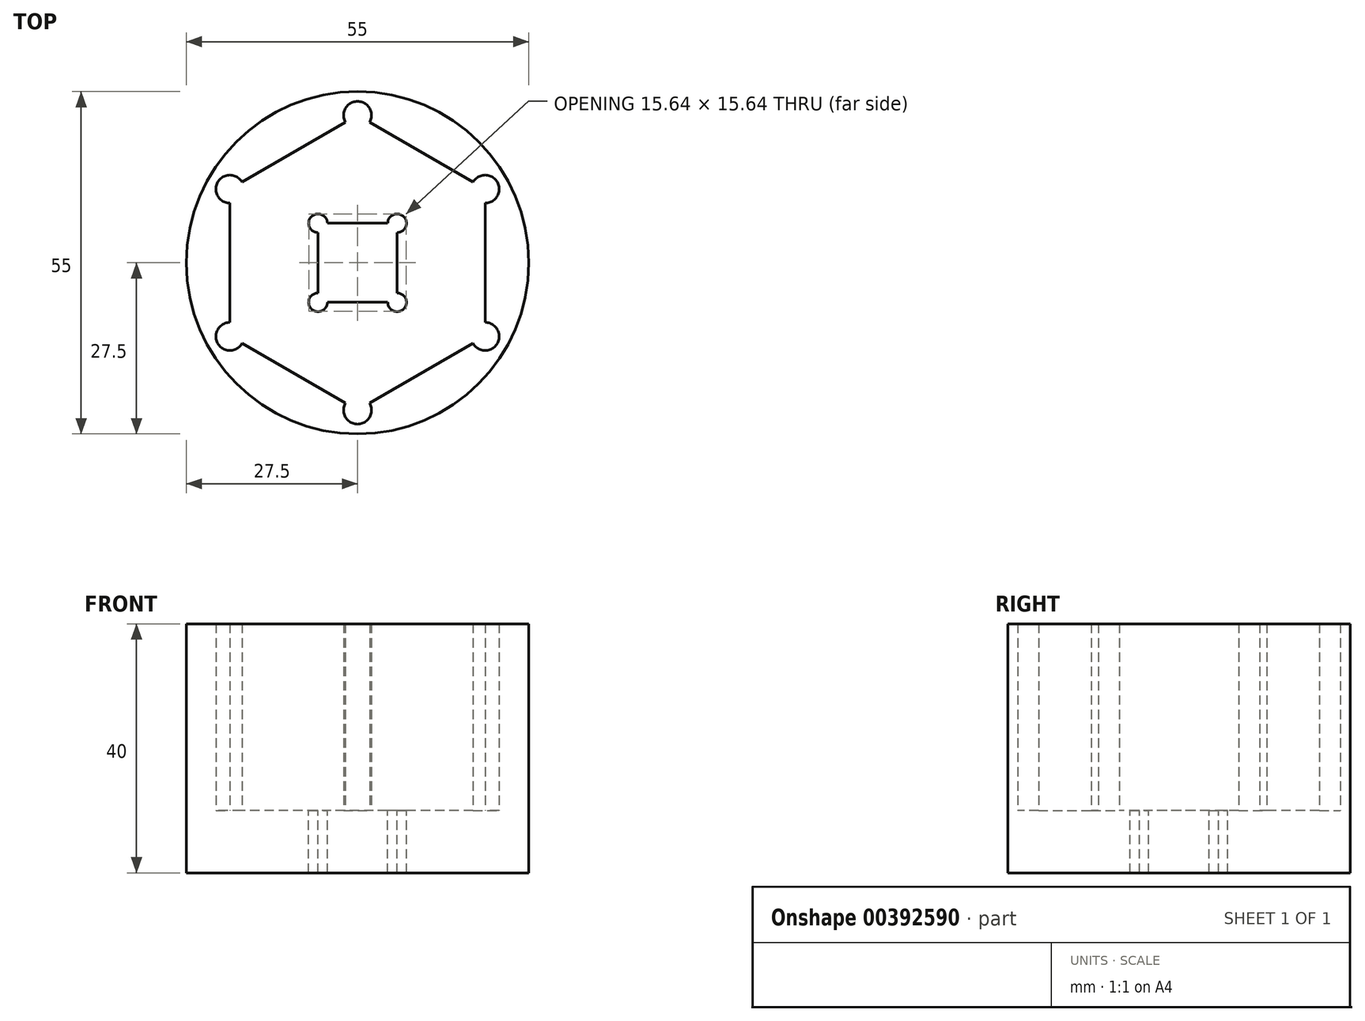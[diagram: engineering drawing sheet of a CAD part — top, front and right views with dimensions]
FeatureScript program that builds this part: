
annotation { "Feature Type Name" : "Feature", "Feature Type Description" : "" }
export const myFeature = defineFeature(function(context is Context, id is Id, definition is map)
    precondition{}
    {
        {
            var Q0;
            Q0=qCreatedBy(makeId("Top.planeOp"),FACE);
            var sketch = newSketch(context, id + "F0", { "sketchPlane" : qUnion([Q0])});
            skCircle(sketch, "E0", {"center": v(0, 0) * mm, "radius": 27.5 * mm});
            skCircle(sketch, "E1.cCircle", {"center": v(0, 0) * mm, "radius": 20.5 * mm, "construction": true});
            skLineSegment(sketch, "E1.0", {"start": v(20.5, 11.84) * mm, "end": v(20.5, -11.84) * mm});
            skLineSegment(sketch, "E1.1", {"start": v(20.5, -11.84) * mm, "end": v(0, -23.67) * mm});
            skLineSegment(sketch, "E1.2", {"start": v(0, -23.67) * mm, "end": v(-20.5, -11.84) * mm});
            skLineSegment(sketch, "E1.3", {"start": v(-20.5, -11.84) * mm, "end": v(-20.5, 11.84) * mm});
            skLineSegment(sketch, "E1.4", {"start": v(-20.5, 11.84) * mm, "end": v(0, 23.67) * mm});
            skLineSegment(sketch, "E1.5", {"start": v(0, 23.67) * mm, "end": v(20.5, 11.84) * mm});
            skPoint(sketch, "E1.0.midPoint", {"position": v(20.5, 0) * mm});
            skCircle(sketch, "E2", {"center": v(-20.5, -11.84) * mm, "radius": 2.25 * mm});
            skCircle(sketch, "E3", {"center": v(-20.5, 11.84) * mm, "radius": 2.25 * mm});
            skCircle(sketch, "E4", {"center": v(0, 23.67) * mm, "radius": 2.25 * mm});
            skCircle(sketch, "E5", {"center": v(20.5, 11.84) * mm, "radius": 2.25 * mm});
            skCircle(sketch, "E6", {"center": v(20.5, -11.84) * mm, "radius": 2.25 * mm});
            skCircle(sketch, "E7", {"center": v(0, -23.67) * mm, "radius": 2.25 * mm});
            skCircle(sketch, "E8", {"center": v(-16.6, -9.59) * mm, "radius": 3.9 * mm, "construction": true});
            skPoint(sketch, "E9", {"position": v(-18.55, -12.96) * mm});
            skPoint(sketch, "E10", {"position": v(-20.5, -9.59) * mm});
            skCircle(sketch, "E11", {"center": v(0, 0) * mm, "radius": 20 * mm, "construction": true});
            skLineSegment(sketch, "E12.bottom", {"start": v(6.35, 6.35) * mm, "end": v(-6.35, 6.35) * mm});
            skLineSegment(sketch, "E12.top", {"start": v(6.35, -6.35) * mm, "end": v(-6.35, -6.35) * mm});
            skLineSegment(sketch, "E12.left", {"start": v(6.35, 6.35) * mm, "end": v(6.35, -6.35) * mm});
            skLineSegment(sketch, "E12.right", {"start": v(-6.35, 6.35) * mm, "end": v(-6.35, -6.35) * mm});
            skCircle(sketch, "E13", {"center": v(-6.35, 6.35) * mm, "radius": 1.5 * mm});
            skCircle(sketch, "E14", {"center": v(6.35, 6.35) * mm, "radius": 1.5 * mm});
            skCircle(sketch, "E15", {"center": v(6.35, -6.35) * mm, "radius": 1.5 * mm});
            skCircle(sketch, "E16", {"center": v(-6.35, -6.35) * mm, "radius": 1.5 * mm});
            skCircle(sketch, "E17", {"center": v(0, 0) * mm, "radius": 6 * mm, "construction": true});
            skSolve(sketch);
        }
        {
            var Q0;
            {var subQ19=sQuery(id+"F0.wireOp",EDGE,"E5");var subQ21=sQuery(id+"F0.wireOp",EDGE,"E1.0");var subQ22=makeQuery(id+"F0.imprint","INTERSECT",VERTEX,{"derivedFrom":[subQ21,subQ19]});Q0=makeQuery(id+"F0.imprint","IMPRINT",FACE,{"disambiguationData":[TD([[makeQuery(id+"F0.imprint","IMPRINT",EDGE,{"disambiguationData":[TD([[subQ22,-1.0]])],"derivedFrom":subQ21}),-1.0]])]});}
            var Q1;
            Q1=makeQuery(id+"F0.imprint","IMPRINT",FACE,{"disambiguationData":[TD([[makeQuery(id+"F0.imprint","IMPRINT",EDGE,{"derivedFrom":sQuery(id+"F0.wireOp",EDGE,"E0")}),1.0]])]});
            var Q2;
            {var subQ0=sQuery(id+"F0.wireOp",EDGE,"E1.4");var subQ1=sQuery(id+"F0.wireOp",EDGE,"E1.3");var subQ2=makeQuery(id+"F0.imprint","INTERSECT",VERTEX,{"derivedFrom":[subQ1,subQ0]});Q2=makeQuery(id+"F0.imprint","IMPRINT",FACE,{"disambiguationData":[TD([[makeQuery(id+"F0.imprint","IMPRINT",EDGE,{"disambiguationData":[TD([[subQ2,1.0]])],"derivedFrom":subQ1}),1.0]])]});}
            var Q3;
            {var subQ0=sQuery(id+"F0.wireOp",EDGE,"E1.3");var subQ1=sQuery(id+"F0.wireOp",EDGE,"E1.2");var subQ2=makeQuery(id+"F0.imprint","INTERSECT",VERTEX,{"derivedFrom":[subQ1,subQ0]});Q3=makeQuery(id+"F0.imprint","IMPRINT",FACE,{"disambiguationData":[TD([[makeQuery(id+"F0.imprint","IMPRINT",EDGE,{"disambiguationData":[TD([[subQ2,1.0]])],"derivedFrom":subQ1}),1.0]])]});}
            var Q4;
            {var subQ0=sQuery(id+"F0.wireOp",EDGE,"E1.3");var subQ1=sQuery(id+"F0.wireOp",EDGE,"E1.2");var subQ2=makeQuery(id+"F0.imprint","INTERSECT",VERTEX,{"derivedFrom":[subQ1,subQ0]});Q4=makeQuery(id+"F0.imprint","IMPRINT",FACE,{"disambiguationData":[TD([[makeQuery(id+"F0.imprint","IMPRINT",EDGE,{"disambiguationData":[TD([[subQ2,1.0]])],"derivedFrom":subQ1}),-1.0]])]});}
            var Q5;
            {var subQ0=sQuery(id+"F0.wireOp",EDGE,"E1.4");var subQ1=sQuery(id+"F0.wireOp",EDGE,"E1.3");var subQ2=makeQuery(id+"F0.imprint","INTERSECT",VERTEX,{"derivedFrom":[subQ1,subQ0]});Q5=makeQuery(id+"F0.imprint","IMPRINT",FACE,{"disambiguationData":[TD([[makeQuery(id+"F0.imprint","IMPRINT",EDGE,{"disambiguationData":[TD([[subQ2,1.0]])],"derivedFrom":subQ1}),-1.0]])]});}
            var Q6;
            {var subQ0=sQuery(id+"F0.wireOp",EDGE,"E1.5");var subQ1=sQuery(id+"F0.wireOp",EDGE,"E1.4");var subQ2=makeQuery(id+"F0.imprint","INTERSECT",VERTEX,{"derivedFrom":[subQ1,subQ0]});Q6=makeQuery(id+"F0.imprint","IMPRINT",FACE,{"disambiguationData":[TD([[makeQuery(id+"F0.imprint","IMPRINT",EDGE,{"disambiguationData":[TD([[subQ2,1.0]])],"derivedFrom":subQ1}),-1.0]])]});}
            var Q7;
            {var subQ0=sQuery(id+"F0.wireOp",EDGE,"E1.5");var subQ1=sQuery(id+"F0.wireOp",EDGE,"E1.4");var subQ2=makeQuery(id+"F0.imprint","INTERSECT",VERTEX,{"derivedFrom":[subQ1,subQ0]});Q7=makeQuery(id+"F0.imprint","IMPRINT",FACE,{"disambiguationData":[TD([[makeQuery(id+"F0.imprint","IMPRINT",EDGE,{"disambiguationData":[TD([[subQ2,1.0]])],"derivedFrom":subQ1}),1.0]])]});}
            var Q8;
            {var subQ0=sQuery(id+"F0.wireOp",EDGE,"E1.5");var subQ1=sQuery(id+"F0.wireOp",EDGE,"E1.0");var subQ2=makeQuery(id+"F0.imprint","INTERSECT",VERTEX,{"derivedFrom":[subQ1,subQ0]});Q8=makeQuery(id+"F0.imprint","IMPRINT",FACE,{"disambiguationData":[TD([[makeQuery(id+"F0.imprint","IMPRINT",EDGE,{"disambiguationData":[TD([[subQ2,-1.0]])],"derivedFrom":subQ1}),-1.0]])]});}
            var Q9;
            {var subQ0=sQuery(id+"F0.wireOp",EDGE,"E1.5");var subQ1=sQuery(id+"F0.wireOp",EDGE,"E1.0");var subQ2=makeQuery(id+"F0.imprint","INTERSECT",VERTEX,{"derivedFrom":[subQ1,subQ0]});Q9=makeQuery(id+"F0.imprint","IMPRINT",FACE,{"disambiguationData":[TD([[makeQuery(id+"F0.imprint","IMPRINT",EDGE,{"disambiguationData":[TD([[subQ2,-1.0]])],"derivedFrom":subQ1}),1.0]])]});}
            var Q10;
            {var subQ0=sQuery(id+"F0.wireOp",EDGE,"E1.1");var subQ1=sQuery(id+"F0.wireOp",EDGE,"E1.0");var subQ2=makeQuery(id+"F0.imprint","INTERSECT",VERTEX,{"derivedFrom":[subQ1,subQ0]});Q10=makeQuery(id+"F0.imprint","IMPRINT",FACE,{"disambiguationData":[TD([[makeQuery(id+"F0.imprint","IMPRINT",EDGE,{"disambiguationData":[TD([[subQ2,1.0]])],"derivedFrom":subQ1}),-1.0]])]});}
            var Q11;
            {var subQ0=sQuery(id+"F0.wireOp",EDGE,"E1.1");var subQ1=sQuery(id+"F0.wireOp",EDGE,"E1.0");var subQ2=makeQuery(id+"F0.imprint","INTERSECT",VERTEX,{"derivedFrom":[subQ1,subQ0]});Q11=makeQuery(id+"F0.imprint","IMPRINT",FACE,{"disambiguationData":[TD([[makeQuery(id+"F0.imprint","IMPRINT",EDGE,{"disambiguationData":[TD([[subQ2,1.0]])],"derivedFrom":subQ1}),1.0]])]});}
            var Q12;
            {var subQ0=sQuery(id+"F0.wireOp",EDGE,"E1.2");var subQ1=sQuery(id+"F0.wireOp",EDGE,"E1.1");var subQ2=makeQuery(id+"F0.imprint","INTERSECT",VERTEX,{"derivedFrom":[subQ1,subQ0]});Q12=makeQuery(id+"F0.imprint","IMPRINT",FACE,{"disambiguationData":[TD([[makeQuery(id+"F0.imprint","IMPRINT",EDGE,{"disambiguationData":[TD([[subQ2,1.0]])],"derivedFrom":subQ1}),-1.0]])]});}
            var Q13;
            {var subQ0=sQuery(id+"F0.wireOp",EDGE,"E1.2");var subQ1=sQuery(id+"F0.wireOp",EDGE,"E1.1");var subQ2=makeQuery(id+"F0.imprint","INTERSECT",VERTEX,{"derivedFrom":[subQ1,subQ0]});Q13=makeQuery(id+"F0.imprint","IMPRINT",FACE,{"disambiguationData":[TD([[makeQuery(id+"F0.imprint","IMPRINT",EDGE,{"disambiguationData":[TD([[subQ2,1.0]])],"derivedFrom":subQ1}),1.0]])]});}
            extrude(context, id + "F1", {"entities" : qUnion([Q0, Q1, Q2, Q3, Q4, Q5, Q6, Q7, Q8, Q9, Q10, Q11, Q12, Q13]), "oppositeDirection" : true, "depth" : 10 * mm});
        }
        {
            var Q0;
            Q0=makeQuery(id+"F0.imprint","IMPRINT",FACE,{"disambiguationData":[TD([[makeQuery(id+"F0.imprint","IMPRINT",EDGE,{"derivedFrom":sQuery(id+"F0.wireOp",EDGE,"E0")}),1.0]])]});
            extrude(context, id + "F2", {"entities" : qUnion([Q0]), "operationType" : NewBodyOperationType.ADD, "depth" : 30 * mm});
        }
    });
